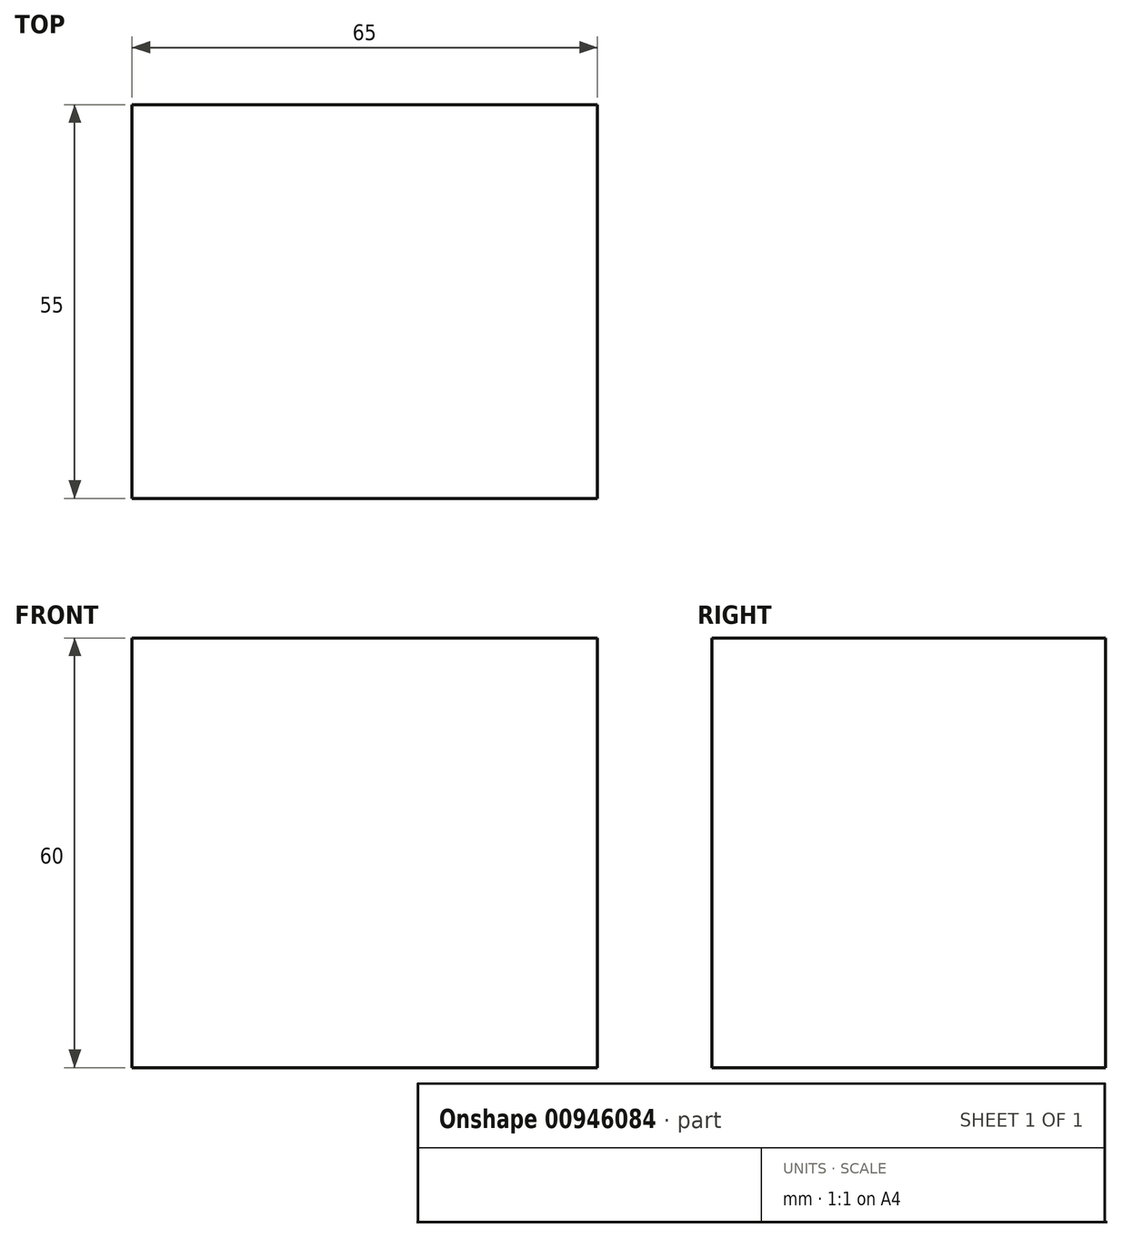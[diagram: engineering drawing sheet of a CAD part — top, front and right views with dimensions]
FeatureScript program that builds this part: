
annotation { "Feature Type Name" : "Feature", "Feature Type Description" : "" }
export const myFeature = defineFeature(function(context is Context, id is Id, definition is map)
    precondition{}
    {
        {
            var Q0;
            Q0=qCreatedBy(makeId("Top.planeOp"),FACE);
            var sketch = newSketch(context, id + "F0", { "sketchPlane" : qUnion([Q0])});
            skLineSegment(sketch, "E0.bottom", {"start": v(-49.38, 33.56) * mm, "end": v(15.62, 33.56) * mm});
            skLineSegment(sketch, "E0.top", {"start": v(-49.38, -21.44) * mm, "end": v(15.62, -21.44) * mm});
            skLineSegment(sketch, "E0.left", {"start": v(-49.38, 33.56) * mm, "end": v(-49.38, -21.44) * mm});
            skLineSegment(sketch, "E0.right", {"start": v(15.62, 33.56) * mm, "end": v(15.62, -21.44) * mm});
            skSolve(sketch);
        }
        {
            var Q0;
            Q0 = qSketchRegion(id + "F0", true);
            extrude(context, id + "F1", {"entities" : qUnion([Q0]), "depth" : 60 * mm, "offsetDistance" : 25 * mm});
        }
    });
